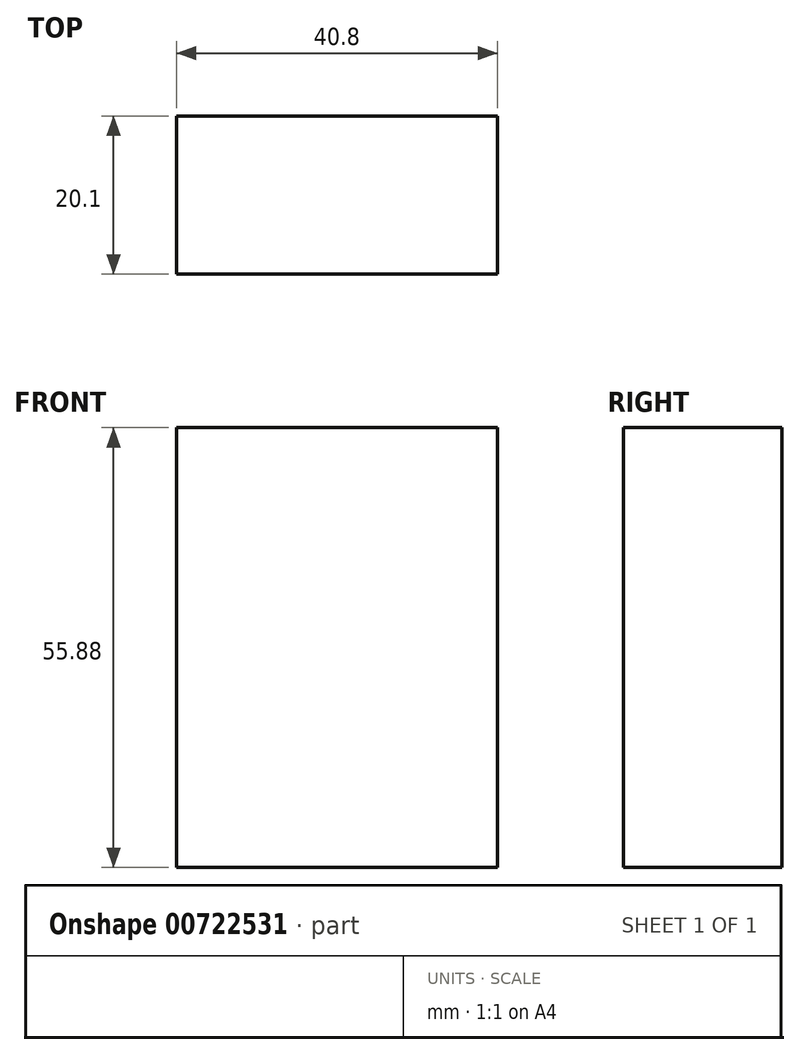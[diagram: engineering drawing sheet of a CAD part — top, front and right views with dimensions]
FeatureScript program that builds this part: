
annotation { "Feature Type Name" : "Feature", "Feature Type Description" : "" }
export const myFeature = defineFeature(function(context is Context, id is Id, definition is map)
    precondition{}
    {
        {
            var Q0;
            Q0=qCreatedBy(makeId("Top.planeOp"),FACE);
            var sketch = newSketch(context, id + "F0", { "sketchPlane" : qUnion([Q0])});
            skLineSegment(sketch, "E0.bottom", {"start": v(0, 0) * mm, "end": v(40.8, 0) * mm});
            skLineSegment(sketch, "E0.top", {"start": v(0, -20.1) * mm, "end": v(40.8, -20.1) * mm});
            skLineSegment(sketch, "E0.left", {"start": v(0, 0) * mm, "end": v(0, -20.1) * mm});
            skLineSegment(sketch, "E0.right", {"start": v(40.8, 0) * mm, "end": v(40.8, -20.1) * mm});
            skSolve(sketch);
        }
        {
            var Q0;
            Q0=makeQuery(id+"F0.imprint","IMPRINT",FACE,{"disambiguationData":[TD([[makeQuery(id+"F0.imprint","IMPRINT",EDGE,{"derivedFrom":sQuery(id+"F0.wireOp",EDGE,"E0.bottom")}),-1.0]])]});
            extrude(context, id + "F1", {"entities" : qUnion([Q0]), "depth" : 55.88 * mm, "offsetDistance" : 25.4 * mm});
        }
    });
